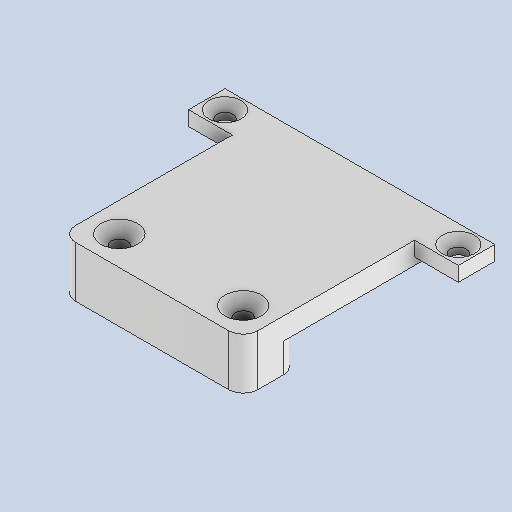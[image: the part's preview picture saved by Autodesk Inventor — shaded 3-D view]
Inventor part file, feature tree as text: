
AUTODESK INVENTOR PART (.ipt)
format: ipt  version: 2025 (Build 290162010, 162A)  size: 215,040 bytes
history: native  units: mm
features: sketch x5, extrude x3, hole x2, fillet x1
ambient origin geometry x8: Origin, YZ Plane, XZ Plane, XY Plane, X Axis, Y Axis, Z Axis, Center Point
bodies: Volumenkörper1 (feature_tree)
feature tree (11):
  extrude  "Extrusion1"  Depth=25.0mm
  extrude  "Extrusion2"  Depth=3.0mm TaperAngle=0.0deg
  hole  "Bohrung1"  [1 undecoded]
  fillet  "Rundung1"  Radius=4.0mm
  extrude  "Extrusion3"  Depth=5.0mm
  hole  "Bohrung2"  [1 undecoded]
  sketch  "Skizze1"  dims[d1=7.5mm d2=25.0mm]
  sketch  "Skizze2"  dims[d4=4.0mm d5=0.0mm d6=3.0mm d7=0.0mm]
  sketch  "Skizze3"  dims[d8=2.2mm d9=6.0mm d10=5.0mm d11=2.0mm d12=90.0deg d13=8.0mm d14=20.594885mm d25=28.5mm d26=4.0mm]
  sketch  "Skizze4"  dims[d27=2.0mm d28=5.0mm]
  sketch  "Skizze5"  dims[d29=5.0mm d30=5.0mm d31=6.0mm d32=2.0mm d33=0.0mm d34=2.5mm d35=2.2mm d36=6.0mm d37=4.4mm d38=2.0mm d39=90.0deg d40=8.0mm d41=20.594885mm d42=2.5mm d43=2.5mm]
note: 2 required parameter values undecoded (feature->parameter linkage not recoverable at this tier; creation-order binding heuristic only, values carry confidence <= 0.55)
